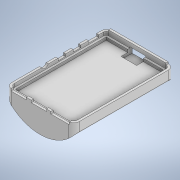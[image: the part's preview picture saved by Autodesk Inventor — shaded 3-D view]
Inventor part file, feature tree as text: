
AUTODESK INVENTOR PART (.ipt)
format: ipt  version: 2022 (Build 260153000, 153)  size: 225,792 bytes
history: native  units: mm
features: other x3, extrude x2, sketch x2, projected_geometry x1
ambient origin geometry x8: Origin, YZ Plane, XZ Plane, XY Plane, X Axis, Y Axis, Z Axis, Center Point
bodies: Solid1 (feature_tree)
feature tree (8):
  other  "piholder-proto-v5.ipt"
  extrude  "Extrusion1"  Depth=38.45mm
  extrude  "Extrusion2"  TaperAngle=0.0deg  [1 undecoded]
  other  "Solid1::piholder-proto-v5.ipt"
  other  "TaggingFeature1"
  sketch  "Sketch1"  dims[d0=10.0mm d1=38.45mm]
  sketch  "Sketch3"  dims[d2=89.5mm d3=0.0mm d4=0.0mm d5=0.0mm]
  projected_geometry  "Projected Loop1"
note: 1 required parameter value undecoded (feature->parameter linkage not recoverable at this tier; creation-order binding heuristic only, values carry confidence <= 0.55)
